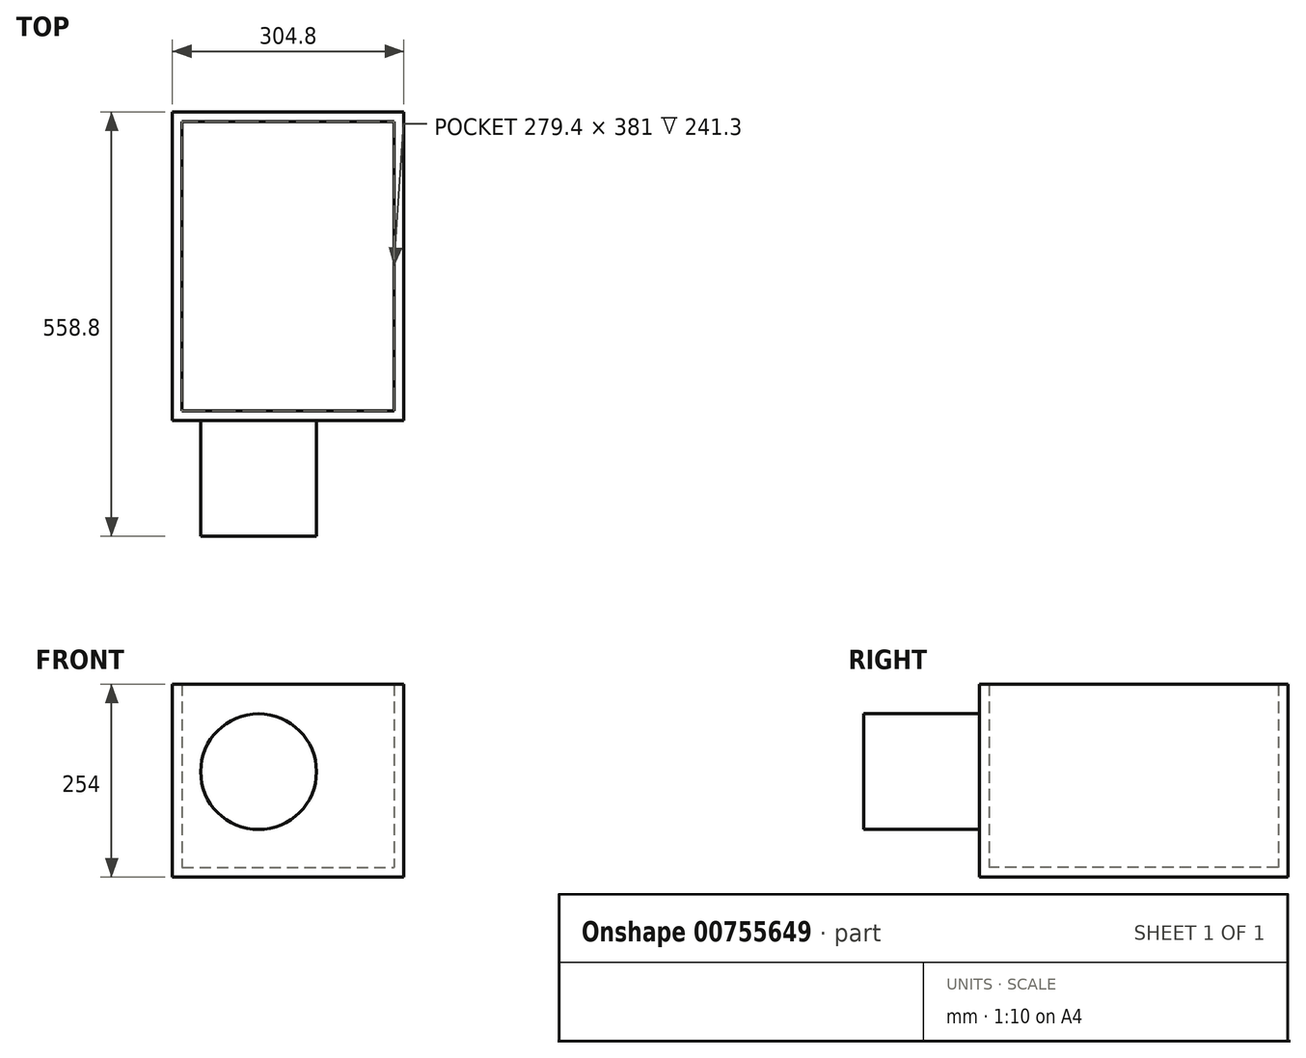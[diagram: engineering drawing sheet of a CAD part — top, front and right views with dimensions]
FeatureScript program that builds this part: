
annotation { "Feature Type Name" : "Feature", "Feature Type Description" : "" }
export const myFeature = defineFeature(function(context is Context, id is Id, definition is map)
    precondition{}
    {
        {
            var Q0;
            Q0=qCreatedBy(makeId("Top.planeOp"),FACE);
            var sketch = newSketch(context, id + "F0", { "sketchPlane" : qUnion([Q0])});
            skLineSegment(sketch, "E0.bottom", {"start": v(-244.89, 239.74) * mm, "end": v(59.91, 239.74) * mm});
            skLineSegment(sketch, "E0.top", {"start": v(-244.89, -166.66) * mm, "end": v(59.91, -166.66) * mm});
            skLineSegment(sketch, "E0.left", {"start": v(-244.89, 239.74) * mm, "end": v(-244.89, -166.66) * mm});
            skLineSegment(sketch, "E0.right", {"start": v(59.91, 239.74) * mm, "end": v(59.91, -166.66) * mm});
            skSolve(sketch);
        }
        {
            var Q0;
            Q0=makeQuery(id+"F0.imprint","IMPRINT",FACE,{"disambiguationData":[TD([[makeQuery(id+"F0.imprint","IMPRINT",EDGE,{"derivedFrom":sQuery(id+"F0.wireOp",EDGE,"E0.bottom")}),-1.0]])]});
            extrude(context, id + "F1", {"entities" : qUnion([Q0]), "depth" : 254 * mm, "offsetDistance" : 25.4 * mm});
        }
        {
            var Q0;
            Q0=makeQuery(id+"F1.opExtrude","CAP_FACE",FACE,{"disambiguationData":[OSD([sQuery(id+"F0.wireOp",EDGE,"E0.bottom"),sQuery(id+"F0.wireOp",EDGE,"E0.top"),sQuery(id+"F0.wireOp",EDGE,"E0.left"),sQuery(id+"F0.wireOp",EDGE,"E0.right")])],"isStart":false});
            shell(context, id + "F2", {"entities" : qUnion([Q0]), "thickness" : 12.7 * mm});
        }
        {
            var Q0;
            Q0=makeQuery(id+"F1.opExtrude","SWEPT_FACE",FACE,{"disambiguationData":[OSD([sQuery(id+"F0.wireOp",EDGE,"E0.top")])]});
            var sketch = newSketch(context, id + "F3", { "sketchPlane" : qUnion([Q0])});
            skCircle(sketch, "E1", {"center": v(-131.48, 138.83) * mm, "radius": 76.2 * mm});
            skSolve(sketch);
        }
        {
            var Q0;
            Q0=makeQuery(id+"F3.imprint","IMPRINT",FACE,{"disambiguationData":[TD([[makeQuery(id+"F3.imprint","IMPRINT",EDGE,{"derivedFrom":sQuery(id+"F3.wireOp",EDGE,"E1")}),1.0]])]});
            extrude(context, id + "F4", {"entities" : qUnion([Q0]), "operationType" : NewBodyOperationType.ADD, "depth" : 152.4 * mm, "offsetDistance" : 25.4 * mm});
        }
    });
